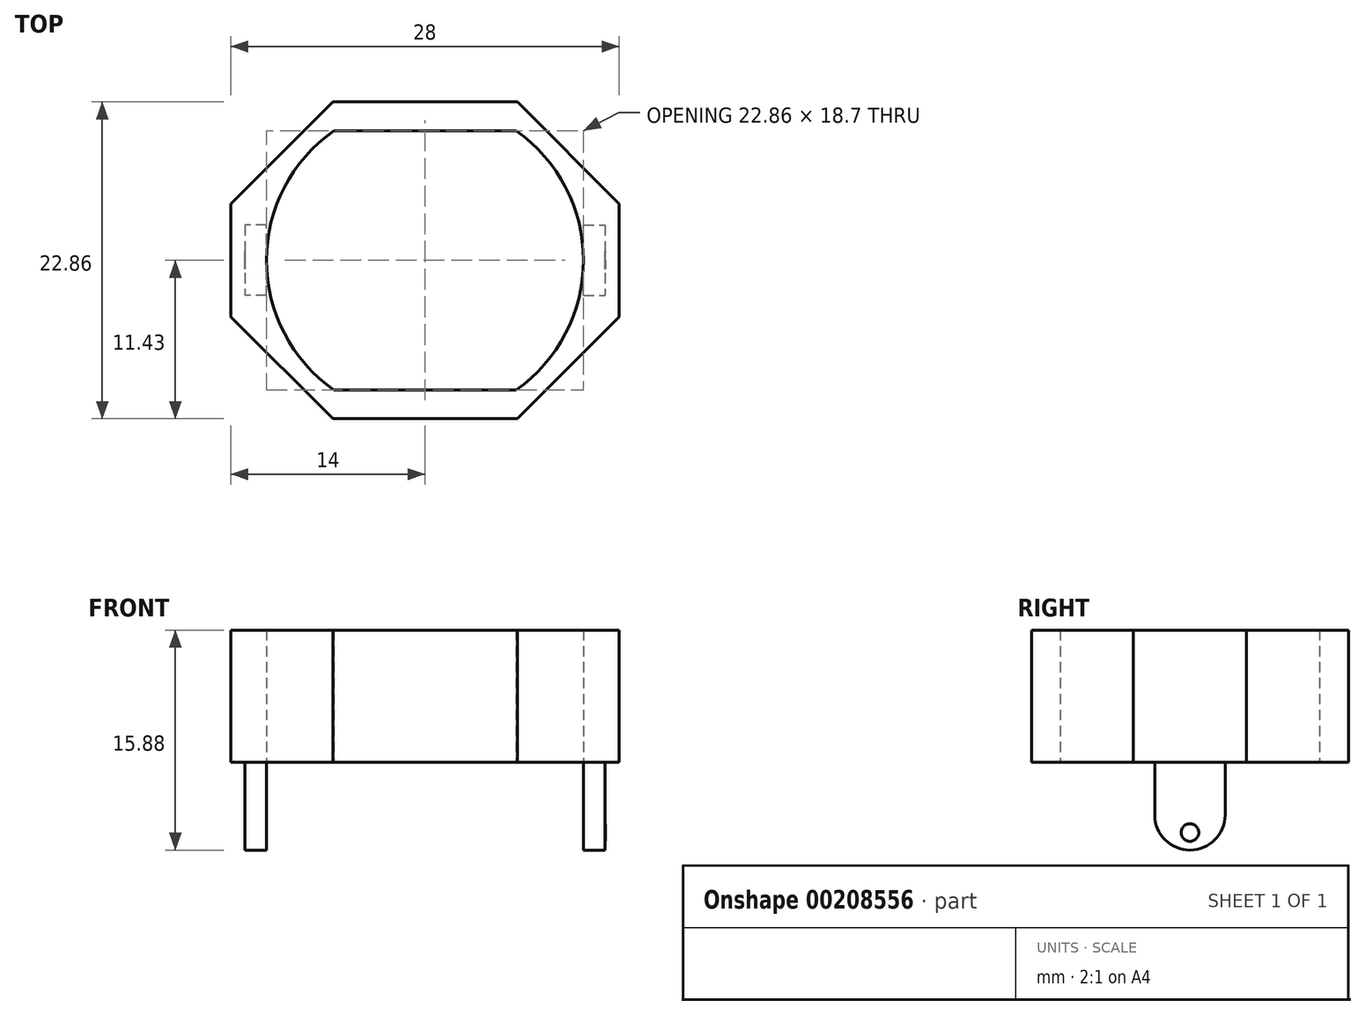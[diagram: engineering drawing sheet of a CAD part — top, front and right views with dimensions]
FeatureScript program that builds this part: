
annotation { "Feature Type Name" : "Feature", "Feature Type Description" : "" }
export const myFeature = defineFeature(function(context is Context, id is Id, definition is map)
    precondition{}
    {
        {
            var Q0;
            Q0=qCreatedBy(makeId("Top.planeOp"),FACE);
            var sketch = newSketch(context, id + "F0", { "sketchPlane" : qUnion([Q0])});
            skArc(sketch, "E0", {"start": v(11.43, 0) * mm, "mid": v(10.14, 5.27) * mm, "end": v(6.57, 9.35) * mm});
            skLineSegment(sketch, "E1", {"start": v(0, 9.35) * mm, "end": v(6.57, 9.35) * mm});
            skArc(sketch, "E2.MirrorCS", {"start": v(-11.43, 0) * mm, "mid": v(-10.14, 5.27) * mm, "end": v(-6.57, 9.35) * mm});
            skLineSegment(sketch, "E3.MirrorCS", {"start": v(0, 9.35) * mm, "end": v(-6.57, 9.35) * mm});
            skLineSegment(sketch, "E4.MirrorCS", {"start": v(0, -9.35) * mm, "end": v(6.57, -9.35) * mm});
            skArc(sketch, "E5.MirrorCS", {"start": v(-11.43, 0) * mm, "mid": v(-10.14, -5.27) * mm, "end": v(-6.57, -9.35) * mm});
            skLineSegment(sketch, "E6.MirrorCS", {"start": v(0, -9.35) * mm, "end": v(-6.57, -9.35) * mm});
            skArc(sketch, "E7.MirrorCS", {"start": v(11.43, 0) * mm, "mid": v(10.14, -5.27) * mm, "end": v(6.57, -9.35) * mm});
            skLineSegment(sketch, "E8", {"start": v(0, 11.43) * mm, "end": v(6.65, 11.43) * mm});
            skLineSegment(sketch, "E9", {"start": v(6.65, 11.43) * mm, "end": v(14, 4.08) * mm});
            skLineSegment(sketch, "E10", {"start": v(14, 4.08) * mm, "end": v(14, 0) * mm});
            skLineSegment(sketch, "E11.MirrorCS", {"start": v(-6.65, 11.43) * mm, "end": v(-14, 4.08) * mm});
            skLineSegment(sketch, "E12.MirrorCS", {"start": v(0, 11.43) * mm, "end": v(-6.65, 11.43) * mm});
            skLineSegment(sketch, "E13.MirrorCS", {"start": v(-14, 4.08) * mm, "end": v(-14, 0) * mm});
            skLineSegment(sketch, "E14.MirrorCS", {"start": v(14, -4.08) * mm, "end": v(14, 0) * mm});
            skLineSegment(sketch, "E15.MirrorCS", {"start": v(6.65, -11.43) * mm, "end": v(14, -4.08) * mm});
            skLineSegment(sketch, "E16.MirrorCS", {"start": v(0, -11.43) * mm, "end": v(6.65, -11.43) * mm});
            skLineSegment(sketch, "E17.MirrorCS", {"start": v(0, -11.43) * mm, "end": v(-6.65, -11.43) * mm});
            skLineSegment(sketch, "E18.MirrorCS", {"start": v(-6.65, -11.43) * mm, "end": v(-14, -4.08) * mm});
            skLineSegment(sketch, "E19.MirrorCS", {"start": v(-14, -4.08) * mm, "end": v(-14, 0) * mm});
            skSolve(sketch);
        }
        {
            var Q0;
            Q0=makeQuery(id+"F0.imprint","IMPRINT",FACE,{"disambiguationData":[TD([[makeQuery(id+"F0.imprint","IMPRINT",EDGE,{"derivedFrom":sQuery(id+"F0.wireOp",EDGE,"E0")}),-1.0]])]});
            extrude(context, id + "F1", {"entities" : qUnion([Q0]), "depth" : 19.05 * mm});
        }
        {
            var Q0;
            Q0=qCreatedBy(makeId("Top.planeOp"),FACE);
            var sketch = newSketch(context, id + "F2", { "sketchPlane" : qUnion([Q0])});
            skPoint(sketch, "E20", {"position": v(11.43, 0) * mm});
            skLineSegment(sketch, "E21", {"start": v(13, 0) * mm, "end": v(13, 2.54) * mm});
            skLineSegment(sketch, "E22", {"start": v(11.43, 2.54) * mm, "end": v(13, 2.54) * mm});
            skLineSegment(sketch, "E23.MirrorCS", {"start": v(11.43, 0) * mm, "end": v(11.43, -2.54) * mm});
            skLineSegment(sketch, "E24.MirrorCS", {"start": v(13, 0) * mm, "end": v(13, -2.54) * mm});
            skLineSegment(sketch, "E25.MirrorCS", {"start": v(11.43, -2.54) * mm, "end": v(13, -2.54) * mm});
            skLineSegment(sketch, "E26", {"start": v(11.43, 0) * mm, "end": v(11.43, 2.54) * mm});
            skSolve(sketch);
        }
        {
            var Q0;
            Q0=makeQuery(id+"F2.imprint","IMPRINT",FACE,{"disambiguationData":[TD([[makeQuery(id+"F2.imprint","IMPRINT",EDGE,{"derivedFrom":sQuery(id+"F2.wireOp",EDGE,"E21")}),1.0]])]});
            extrude(context, id + "F3", {"entities" : qUnion([Q0]), "operationType" : NewBodyOperationType.ADD, "oppositeDirection" : true, "depth" : 6.35 * mm});
        }
        {
            var Q0;
            Q0=makeQuery(id+"F3.opExtrude","SWEPT_FACE",FACE,{"disambiguationData":[OSD([sQuery(id+"F2.wireOp",EDGE,"E21"),sQuery(id+"F2.wireOp",EDGE,"E24.MirrorCS")])]});
            var sketch = newSketch(context, id + "F4", { "sketchPlane" : qUnion([Q0])});
            skCircle(sketch, "E27", {"center": v(0, -5.08) * mm, "radius": 0.64 * mm});
            skPoint(sketch, "E27.centerSnap0", {"position": v(0, -6.35) * mm});
            skSolve(sketch);
        }
        {
            var Q0;
            Q0=makeQuery(id+"F4.imprint","IMPRINT",FACE,{"disambiguationData":[TD([[makeQuery(id+"F4.imprint","IMPRINT",EDGE,{"derivedFrom":sQuery(id+"F4.wireOp",EDGE,"E27")}),1.0]])]});
            extrude(context, id + "F5", {"entities" : qUnion([Q0]), "operationType" : NewBodyOperationType.ADD, "depth" : 0.12 / 50.8 * mm});
        }
        {
            var Q0;
            Q0=makeQuery(id+"FM54qVA6fSZPACi_2.opPattern","COPY",EDGE,{"derivedFrom":makeQuery(id+"F3.opExtrude","CAP_EDGE",EDGE,{"disambiguationData":[OSD([sQuery(id+"F2.wireOp",EDGE,"E25.MirrorCS")])],"isStart":false}),"instanceName":"1"});
            var Q1;
            Q1=makeQuery(id+"FM54qVA6fSZPACi_2.opPattern","COPY",EDGE,{"derivedFrom":makeQuery(id+"F3.opExtrude","CAP_EDGE",EDGE,{"disambiguationData":[OSD([sQuery(id+"F2.wireOp",EDGE,"E22")])],"isStart":false}),"instanceName":"1"});
            var Q2;
            Q2=makeQuery(id+"F3.opExtrude","CAP_EDGE",EDGE,{"disambiguationData":[OSD([sQuery(id+"F2.wireOp",EDGE,"E25.MirrorCS")])],"isStart":false});
            var Q3;
            Q3=makeQuery(id+"F3.opExtrude","CAP_EDGE",EDGE,{"disambiguationData":[OSD([sQuery(id+"F2.wireOp",EDGE,"E22")])],"isStart":false});
            fillet(context, id + "F6", {"entities" : qUnion([Q0, Q1, Q2, Q3]), "radius" : 2.54 * mm, "tangentPropagation" : true, "allowEdgeOverflow" : false});
        }
        {
            var Q0;
            Q0=makeQuery(id+"F5.opExtrude","CAP_EDGE",EDGE,{"disambiguationData":[OSD([sQuery(id+"F4.wireOp",EDGE,"E27")])],"isStart":false});
            var Q1;
            Q1=makeQuery(id+"FM54qVA6fSZPACi_2.opPattern","COPY",EDGE,{"derivedFrom":makeQuery(id+"F5.opExtrude","CAP_EDGE",EDGE,{"disambiguationData":[OSD([sQuery(id+"F4.wireOp",EDGE,"E27")])],"isStart":false}),"instanceName":"1"});
            fillet(context, id + "F7", {"entities" : qUnion([Q0, Q1]), "radius" : 0.64 * mm, "tangentPropagation" : true, "allowEdgeOverflow" : false});
        }
        {
            var Q0;
            Q0=makeQuery(id+"F1.opExtrude","CAP_FACE",FACE,{"disambiguationData":[OSD([sQuery(id+"F0.wireOp",EDGE,"E0"),sQuery(id+"F0.wireOp",EDGE,"E1"),sQuery(id+"F0.wireOp",EDGE,"E2.MirrorCS"),sQuery(id+"F0.wireOp",EDGE,"E3.MirrorCS"),sQuery(id+"F0.wireOp",EDGE,"E4.MirrorCS"),sQuery(id+"F0.wireOp",EDGE,"E5.MirrorCS"),sQuery(id+"F0.wireOp",EDGE,"E6.MirrorCS"),sQuery(id+"F0.wireOp",EDGE,"E7.MirrorCS"),sQuery(id+"F0.wireOp",EDGE,"E8"),sQuery(id+"F0.wireOp",EDGE,"E9"),sQuery(id+"F0.wireOp",EDGE,"E10"),sQuery(id+"F0.wireOp",EDGE,"E11.MirrorCS"),sQuery(id+"F0.wireOp",EDGE,"E12.MirrorCS"),sQuery(id+"F0.wireOp",EDGE,"E13.MirrorCS"),sQuery(id+"F0.wireOp",EDGE,"E14.MirrorCS"),sQuery(id+"F0.wireOp",EDGE,"E15.MirrorCS"),sQuery(id+"F0.wireOp",EDGE,"E16.MirrorCS"),sQuery(id+"F0.wireOp",EDGE,"E17.MirrorCS"),sQuery(id+"F0.wireOp",EDGE,"E18.MirrorCS"),sQuery(id+"F0.wireOp",EDGE,"E19.MirrorCS")])],"isStart":false});
            var sketch = newSketch(context, id + "F8", { "sketchPlane" : qUnion([Q0])});
            skPoint(sketch, "E28", {"position": v(12.43, 2.54) * mm});
            skPoint(sketch, "E29", {"position": v(14, 0) * mm});
            skLineSegment(sketch, "E30.bottom", {"start": v(12.43, 2.54) * mm, "end": v(14, 2.54) * mm});
            skLineSegment(sketch, "E30.left", {"start": v(12.43, 2.54) * mm, "end": v(12.43, 0) * mm});
            skLineSegment(sketch, "E30.right", {"start": v(14, 2.54) * mm, "end": v(14, 0) * mm});
            skLineSegment(sketch, "E31.MirrorCS", {"start": v(14, -2.54) * mm, "end": v(14, 0) * mm});
            skLineSegment(sketch, "E32.MirrorCS", {"start": v(12.43, -2.54) * mm, "end": v(14, -2.54) * mm});
            skLineSegment(sketch, "E33.MirrorCS", {"start": v(12.43, -2.54) * mm, "end": v(12.43, 0) * mm});
            skSolve(sketch);
        }
        {
            var Q0;
            Q0=makeQuery(id+"F8.imprint","IMPRINT",FACE,{"disambiguationData":[TD([[makeQuery(id+"F8.imprint","IMPRINT",EDGE,{"derivedFrom":sQuery(id+"F8.wireOp",EDGE,"E30.bottom")}),-1.0]])]});
            extrude(context, id + "F9", {"entities" : qUnion([Q0]), "operationType" : NewBodyOperationType.ADD, "depth" : 6.35 * mm});
        }
        {
            var Q0;
            Q0=makeQuery(id+"F9.boolean.opBoolean","MERGE",FACE,{"derivedFrom":[makeQuery(id+"F1.opExtrude","SWEPT_FACE",FACE,{"disambiguationData":[OSD([sQuery(id+"F0.wireOp",EDGE,"E10"),sQuery(id+"F0.wireOp",EDGE,"E14.MirrorCS")])]}),makeQuery(id+"F9.opExtrude","SWEPT_FACE",FACE,{"disambiguationData":[OSD([sQuery(id+"F8.wireOp",EDGE,"E30.right"),sQuery(id+"F8.wireOp",EDGE,"E31.MirrorCS")])]})]});
            var sketch = newSketch(context, id + "F10", { "sketchPlane" : qUnion([Q0])});
            skPoint(sketch, "E34", {"position": v(0, 22.86) * mm});
            skPoint(sketch, "E34.positionSnap0", {"position": v(0, 25.4) * mm});
            skSolve(sketch);
        }
        {
            var Q0;
            Q0=sQuery(id+"F10.wireOp",VERTEX,"E34");
            var Q1;
            Q1=makeQuery(id+"F1.opExtrude","SWEPT_BODY",BODY,{"disambiguationData":[OSD([sQuery(id+"F0.wireOp",EDGE,"E0"),sQuery(id+"F0.wireOp",EDGE,"E1"),sQuery(id+"F0.wireOp",EDGE,"E2.MirrorCS"),sQuery(id+"F0.wireOp",EDGE,"E3.MirrorCS"),sQuery(id+"F0.wireOp",EDGE,"E4.MirrorCS"),sQuery(id+"F0.wireOp",EDGE,"E5.MirrorCS"),sQuery(id+"F0.wireOp",EDGE,"E6.MirrorCS"),sQuery(id+"F0.wireOp",EDGE,"E7.MirrorCS"),sQuery(id+"F0.wireOp",EDGE,"E8"),sQuery(id+"F0.wireOp",EDGE,"E9"),sQuery(id+"F0.wireOp",EDGE,"E10"),sQuery(id+"F0.wireOp",EDGE,"E11.MirrorCS"),sQuery(id+"F0.wireOp",EDGE,"E12.MirrorCS"),sQuery(id+"F0.wireOp",EDGE,"E13.MirrorCS"),sQuery(id+"F0.wireOp",EDGE,"E14.MirrorCS"),sQuery(id+"F0.wireOp",EDGE,"E15.MirrorCS"),sQuery(id+"F0.wireOp",EDGE,"E16.MirrorCS"),sQuery(id+"F0.wireOp",EDGE,"E17.MirrorCS"),sQuery(id+"F0.wireOp",EDGE,"E18.MirrorCS"),sQuery(id+"F0.wireOp",EDGE,"E19.MirrorCS")])]});
            hole(context, id + "F11", {"style" : HoleStyle.SIMPLE, "endStyle" : HoleEndStyle.THROUGH, "holeDiameter" : 2.54 * mm, "locations" : qUnion([Q0]), "scope" : qUnion([Q1]), "isTappedThrough" : true});
        }
        {
            var Q0;
            Q0=makeQuery(id+"F1.opExtrude","SWEPT_BODY",BODY,{"disambiguationData":[OSD([sQuery(id+"F0.wireOp",EDGE,"E0"),sQuery(id+"F0.wireOp",EDGE,"E1"),sQuery(id+"F0.wireOp",EDGE,"E2.MirrorCS"),sQuery(id+"F0.wireOp",EDGE,"E3.MirrorCS"),sQuery(id+"F0.wireOp",EDGE,"E4.MirrorCS"),sQuery(id+"F0.wireOp",EDGE,"E5.MirrorCS"),sQuery(id+"F0.wireOp",EDGE,"E6.MirrorCS"),sQuery(id+"F0.wireOp",EDGE,"E7.MirrorCS"),sQuery(id+"F0.wireOp",EDGE,"E8"),sQuery(id+"F0.wireOp",EDGE,"E9"),sQuery(id+"F0.wireOp",EDGE,"E10"),sQuery(id+"F0.wireOp",EDGE,"E11.MirrorCS"),sQuery(id+"F0.wireOp",EDGE,"E12.MirrorCS"),sQuery(id+"F0.wireOp",EDGE,"E13.MirrorCS"),sQuery(id+"F0.wireOp",EDGE,"E14.MirrorCS"),sQuery(id+"F0.wireOp",EDGE,"E15.MirrorCS"),sQuery(id+"F0.wireOp",EDGE,"E16.MirrorCS"),sQuery(id+"F0.wireOp",EDGE,"E17.MirrorCS"),sQuery(id+"F0.wireOp",EDGE,"E18.MirrorCS"),sQuery(id+"F0.wireOp",EDGE,"E19.MirrorCS")])]});
            var Q1;
            Q1=qCreatedBy(makeId("Right.planeOp"),FACE);
            mirror(context, id + "F12", {"operationType" : NewBodyOperationType.ADD, "entities" : qUnion([Q0]), "mirrorPlane" : qUnion([Q1])});
        }
        {
            var Q0;
            Q0=makeQuery(id+"F1.opExtrude","SWEPT_FACE",FACE,{"disambiguationData":[OSD([sQuery(id+"F0.wireOp",EDGE,"E1"),sQuery(id+"F0.wireOp",EDGE,"E3.MirrorCS")])]});
            var sketch = newSketch(context, id + "F13", { "sketchPlane" : qUnion([Q0])});
            skLineSegment(sketch, "E35", {"start": v(-6.57, 9.53) * mm, "end": v(6.57, 9.53) * mm});
            skSolve(sketch);
        }
        {
            var Q0;
            Q0=sQuery(id+"F13.wireOp",EDGE,"E35");
            extrude(context, id + "F14", {"bodyType" : ToolBodyType.SURFACE, "surfaceEntities" : qUnion([Q0]), "endBound" : BoundingType.UP_TO_NEXT, "depth" : 25.4 * mm});
        }
        {
            var Q0;
            Q0=makeQuery(id+"F14.opExtrude","SWEPT_FACE",FACE,{"disambiguationData":[OSD([sQuery(id+"F13.wireOp",EDGE,"E35")])]});
            var sketch = newSketch(context, id + "F15", { "sketchPlane" : qUnion([Q0])});
            skPoint(sketch, "E36", {"position": v(0, 0) * mm});
            skSolve(sketch);
        }
        {
            var Q0;
            Q0=sQuery(id+"F15.wireOp",VERTEX,"E36");
            var Q1;
            Q1=makeQuery(id+"F1.opExtrude","SWEPT_BODY",BODY,{"disambiguationData":[OSD([sQuery(id+"F0.wireOp",EDGE,"E0"),sQuery(id+"F0.wireOp",EDGE,"E1"),sQuery(id+"F0.wireOp",EDGE,"E2.MirrorCS"),sQuery(id+"F0.wireOp",EDGE,"E3.MirrorCS"),sQuery(id+"F0.wireOp",EDGE,"E4.MirrorCS"),sQuery(id+"F0.wireOp",EDGE,"E5.MirrorCS"),sQuery(id+"F0.wireOp",EDGE,"E6.MirrorCS"),sQuery(id+"F0.wireOp",EDGE,"E7.MirrorCS"),sQuery(id+"F0.wireOp",EDGE,"E8"),sQuery(id+"F0.wireOp",EDGE,"E9"),sQuery(id+"F0.wireOp",EDGE,"E10"),sQuery(id+"F0.wireOp",EDGE,"E11.MirrorCS"),sQuery(id+"F0.wireOp",EDGE,"E12.MirrorCS"),sQuery(id+"F0.wireOp",EDGE,"E13.MirrorCS"),sQuery(id+"F0.wireOp",EDGE,"E14.MirrorCS"),sQuery(id+"F0.wireOp",EDGE,"E15.MirrorCS"),sQuery(id+"F0.wireOp",EDGE,"E16.MirrorCS"),sQuery(id+"F0.wireOp",EDGE,"E17.MirrorCS"),sQuery(id+"F0.wireOp",EDGE,"E18.MirrorCS"),sQuery(id+"F0.wireOp",EDGE,"E19.MirrorCS")])]});
            hole(context, id + "F16", {"style" : HoleStyle.SIMPLE, "endStyle" : HoleEndStyle.THROUGH, "holeDiameter" : 127 * mm, "locations" : qUnion([Q0]), "scope" : qUnion([Q1]), "isTappedThrough" : true});
        }
        {
            var Q0;
            Q0=makeQuery(id+"F14.opExtrude","SWEPT_BODY",BODY,{"disambiguationData":[OSD([sQuery(id+"F13.wireOp",EDGE,"E35")])]});
            deleteBodies(context, id + "F17", {"entities" : qUnion([Q0])});
        }
    });
